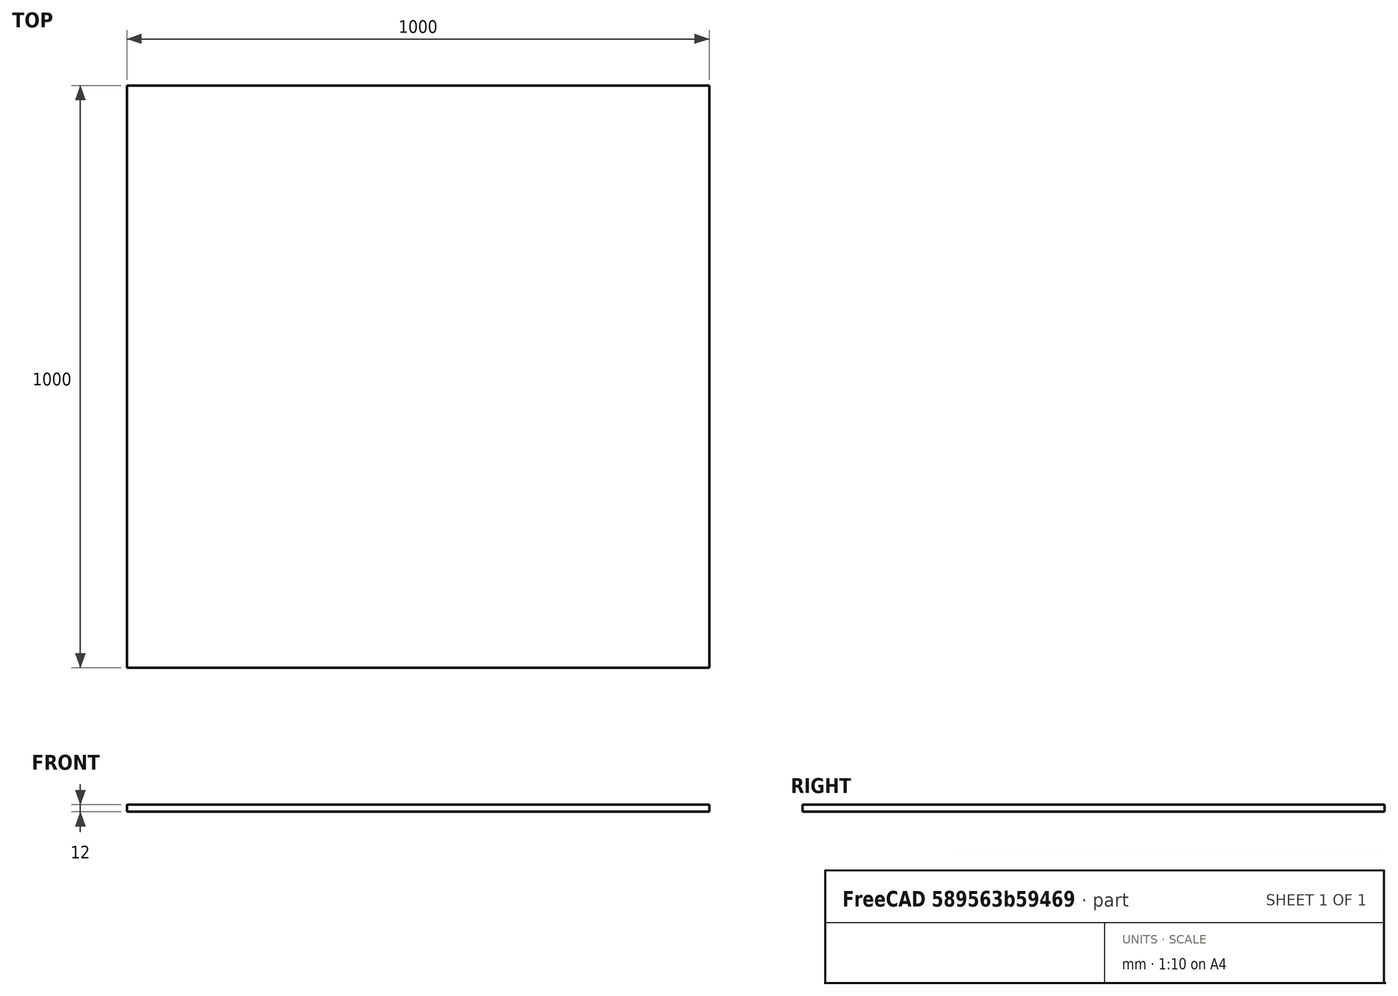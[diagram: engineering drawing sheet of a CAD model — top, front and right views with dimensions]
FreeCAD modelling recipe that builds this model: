
FCSTD DOCUMENT  (FreeCAD 0.16RUnknown)
Label: babyStep
License: All rights reserved
LicenseURL: http://en.wikipedia.org/wiki/All_rights_reserved
objects: Spreadsheet::Sheet×1, Sketcher::SketchObject×1, PartDesign::Pad×1
note: 3 computed .brp shape members not serialized (recipe doc carries the construction recipe); baked Part::Feature solids carry a one-line shape summary decoded from their .brp

FEATURE [Spreadsheet::Sheet] Spreadsheet  label="Equations"
  cells = A1=thickness; B1=thy ; C1(thy)==12mm; A2=length ; B2=len; C2(len)=1000; A3=breadth; B3=brd; C3(brd)=1000; A4=height; B4==hgt; C4(hgt)=1000
FEATURE [Sketcher::SketchObject] Sketch
  Placement = pos=(0,0,0) rot=(1,0,0;3.14159rad)
  expr: Constraints[9] = Equations.brd
  expr: Constraints[10] = Equations.brd
  sketch-geometry (4):
    g0: LineSegment StartX=0 StartY=0 StartZ=0 EndX=1000 EndY=0 EndZ=0
    g1: LineSegment StartX=1000 StartY=0 StartZ=0 EndX=1000 EndY=1000 EndZ=0
    g2: LineSegment StartX=1000 StartY=1000 StartZ=0 EndX=0 EndY=1000 EndZ=0
    g3: LineSegment StartX=0 StartY=1000 StartZ=0 EndX=0 EndY=0 EndZ=0
  constraints (11):
    c: Coincident(g0,g1)
    c: Coincident(g1,g2)
    c: Coincident(g2,g3)
    c: Coincident(g3,g0)
    c: Horizontal(g0)
    c: Horizontal(g2)
    c: Vertical(g1)
    c: Vertical(g3)
    c: Coincident(g0,g-1)
    c: Distance(g1) = 1000
    c: Distance(g0) = 1000
FEATURE [PartDesign::Pad] Pad
  Length = 12
  Length2 = 100
  Placement = pos=(0,0,0) rot=(1,0,0;3.14159rad)
  Sketch = -> Sketch
  Type = 0
  expr: Length = Equations.thy
